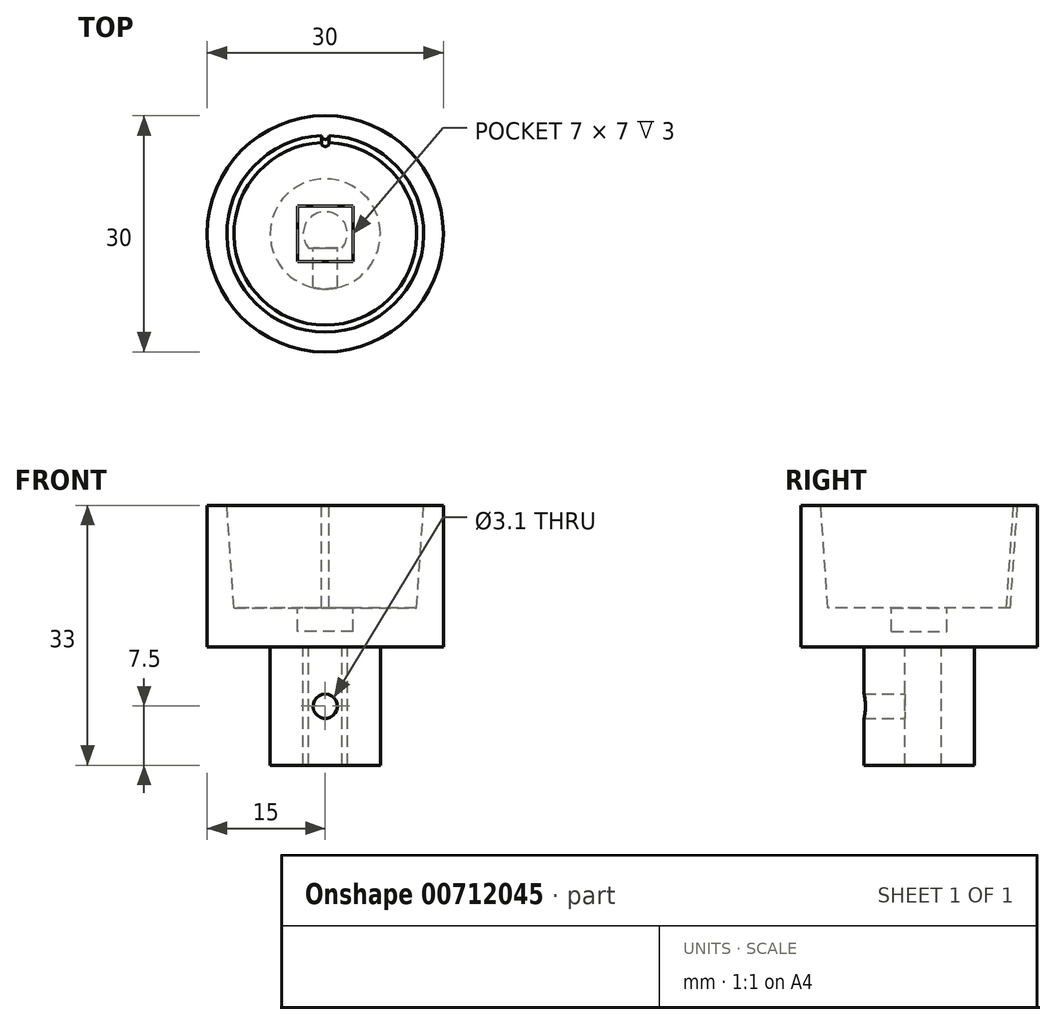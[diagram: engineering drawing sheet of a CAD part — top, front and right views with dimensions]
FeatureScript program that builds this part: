
annotation { "Feature Type Name" : "Feature", "Feature Type Description" : "" }
export const myFeature = defineFeature(function(context is Context, id is Id, definition is map)
    precondition{}
    {
        {
            var Q0;
            Q0=qCreatedBy(makeId("Top.planeOp"),FACE);
            var sketch = newSketch(context, id + "F0", { "sketchPlane" : qUnion([Q0])});
            skLineSegment(sketch, "E0", {"start": v(-2.14, -1.8) * mm, "end": v(2.14, -1.8) * mm});
            skArc(sketch, "E1", {"start": v(-2.14, -1.8) * mm, "mid": v(0, 2.8) * mm, "end": v(2.14, -1.8) * mm});
            skCircle(sketch, "E2", {"center": v(0, 0) * mm, "radius": 15 * mm});
            skCircle(sketch, "E3", {"center": v(0, 0) * mm, "radius": 7 * mm});
            skCircle(sketch, "E4", {"center": v(0, 0) * mm, "radius": 11.6 * mm});
            skSolve(sketch);
        }
        {
            var Q0;
            Q0=makeQuery(id+"F0.imprint","IMPRINT",FACE,{"disambiguationData":[TD([[makeQuery(id+"F0.imprint","IMPRINT",EDGE,{"derivedFrom":sQuery(id+"F0.wireOp",EDGE,"E0")}),-1.0]])]});
            var Q1;
            Q1=sQuery(id+"F0.wireOp",EDGE,"E1");
            var Q2;
            Q2=sQuery(id+"F0.wireOp",EDGE,"E0");
            extrude(context, id + "F1", {"entities" : qUnion([Q0]), "surfaceEntities" : qUnion([Q1, Q2]), "oppositeDirection" : true, "depth" : 15 * mm, "offsetDistance" : 25 * mm});
        }
        {
            var Q0;
            Q0=makeQuery(id+"F0.imprint","IMPRINT",FACE,{"disambiguationData":[TD([[makeQuery(id+"F0.imprint","IMPRINT",EDGE,{"derivedFrom":sQuery(id+"F0.wireOp",EDGE,"E3")}),-1.0]])]});
            var Q1;
            Q1=makeQuery(id+"F0.imprint","IMPRINT",FACE,{"disambiguationData":[TD([[makeQuery(id+"F0.imprint","IMPRINT",EDGE,{"derivedFrom":sQuery(id+"F0.wireOp",EDGE,"E0")}),1.0]])]});
            var Q2;
            Q2=makeQuery(id+"F0.imprint","IMPRINT",FACE,{"disambiguationData":[TD([[makeQuery(id+"F0.imprint","IMPRINT",EDGE,{"derivedFrom":sQuery(id+"F0.wireOp",EDGE,"E0")}),-1.0]])]});
            extrude(context, id + "F2", {"entities" : qUnion([Q0, Q1, Q2]), "operationType" : NewBodyOperationType.ADD, "depth" : 5 * mm, "offsetDistance" : 25 * mm});
        }
        {
            var Q0;
            {var subQ0=sQuery(id+"F0.wireOp",EDGE,"E0");Q0=makeQuery(id+"F2.boolean.opBoolean","MERGE",FACE,{"derivedFrom":[makeQuery(id+"F1.opExtrude","SWEPT_FACE",FACE,{"disambiguationData":[OSD([subQ0])]}),makeQuery(id+"F2.opExtrude","SWEPT_FACE",FACE,{"disambiguationData":[OSD([subQ0])]})]});}
            var sketch = newSketch(context, id + "F3", { "sketchPlane" : qUnion([Q0])});
            skPoint(sketch, "E5", {"position": v(0, -7.5) * mm});
            skSolve(sketch);
        }
        {
            var Q0;
            Q0=sQuery(id+"F3.wireOp",VERTEX,"E5");
            var Q1;
            Q1=makeQuery(id+"F1.opExtrude","SWEPT_BODY",BODY,{"disambiguationData":[OSD([sQuery(id+"F0.wireOp",EDGE,"E0"),sQuery(id+"F0.wireOp",EDGE,"E1"),sQuery(id+"F0.wireOp",EDGE,"E3")])]});
            hole(context, id + "F4", {"style" : HoleStyle.SIMPLE, "endStyle" : HoleEndStyle.THROUGH, "holeDiameter" : 3.1 * mm, "majorDiameter" : 5 * mm, "isTappedThrough" : true, "tappedDepth" : 12 * mm, "tapClearance" : 3, "locations" : qUnion([Q0]), "scope" : qUnion([Q1])});
        }
        {
            var Q0;
            Q0=makeQuery(id+"F2.opExtrude","CAP_FACE",FACE,{"disambiguationData":[OSD([sQuery(id+"F0.wireOp",EDGE,"E4"),sQuery(id+"F0.wireOp",EDGE,"QTVwVzxJ-1bkS-bkWT-XEsq-TVnwtJ6gXQn8")])],"isStart":false});
            var sketch = newSketch(context, id + "F5", { "sketchPlane" : qUnion([Q0])});
            skLineSegment(sketch, "E6.bottom", {"start": v(3.5, -3.5) * mm, "end": v(-3.5, -3.5) * mm});
            skLineSegment(sketch, "E6.top", {"start": v(3.5, 3.5) * mm, "end": v(-3.5, 3.5) * mm});
            skLineSegment(sketch, "E6.left", {"start": v(3.5, -3.5) * mm, "end": v(3.5, 3.5) * mm});
            skLineSegment(sketch, "E6.right", {"start": v(-3.5, -3.5) * mm, "end": v(-3.5, 3.5) * mm});
            skPoint(sketch, "E6.middle", {"position": v(0, 0) * mm});
            skSolve(sketch);
        }
        {
            var Q0;
            Q0=makeQuery(id+"F5.imprint","IMPRINT",FACE,{"disambiguationData":[TD([[makeQuery(id+"F5.imprint","IMPRINT",EDGE,{"derivedFrom":sQuery(id+"F5.wireOp",EDGE,"E6.bottom")}),-1.0]])]});
            extrude(context, id + "F6", {"entities" : qUnion([Q0]), "operationType" : NewBodyOperationType.REMOVE, "oppositeDirection" : true, "depth" : 3 * mm, "offsetDistance" : 25 * mm});
        }
        {
            var Q0;
            Q0=qCreatedBy(makeId("Right.planeOp"),FACE);
            var sketch = newSketch(context, id + "F7", { "sketchPlane" : qUnion([Q0])});
            skLineSegment(sketch, "E7", {"start": v(11.6, 0) * mm, "end": v(15, 0) * mm});
            skLineSegment(sketch, "E8", {"start": v(15, 18) * mm, "end": v(12.5, 18) * mm});
            skLineSegment(sketch, "E9", {"start": v(15, 18) * mm, "end": v(15, 0) * mm});
            skLineSegment(sketch, "E10", {"start": v(11.6, 0) * mm, "end": v(11.6, 5) * mm});
            skLineSegment(sketch, "E11", {"start": v(11.6, 5) * mm, "end": v(12.5, 18) * mm});
            skLineSegment(sketch, "E12", {"start": v(0, 9.96) * mm, "end": v(0, -1.49) * mm, "construction": true});
            skSolve(sketch);
        }
        {
            var Q0;
            Q0=makeQuery(id+"F7.imprint","IMPRINT",FACE,{"disambiguationData":[TD([[makeQuery(id+"F7.imprint","IMPRINT",EDGE,{"derivedFrom":sQuery(id+"F7.wireOp",EDGE,"E7")}),1.0]])]});
            var Q1;
            Q1=sQuery(id+"F7.wireOp",EDGE,"E12");
            revolve(context, id + "F8", {"operationType" : NewBodyOperationType.ADD, "surfaceOperationType" : NewSurfaceOperationType.NEW, "entities" : qUnion([Q0]), "axis" : qUnion([Q1]), "revolveType" : RevolveType.FULL});
        }
        {
            var Q0;
            Q0=makeQuery(id+"F5.imprint","IMPRINT",FACE,{"disambiguationData":[TD([[makeQuery(id+"F5.imprint","IMPRINT",EDGE,{"derivedFrom":sQuery(id+"F5.wireOp",EDGE,"E6.bottom")}),1.0]])]});
            var sketch = newSketch(context, id + "F9", { "sketchPlane" : qUnion([Q0])});
            skCircle(sketch, "E13", {"center": v(0, 0) * mm, "radius": 11.6 * mm, "construction": true});
            skArc(sketch, "E14", {"start": v(-0.5, 11.59) * mm, "mid": v(0, 11.1) * mm, "end": v(0.5, 11.59) * mm});
            skSolve(sketch);
        }
        {
            var Q0;
            Q0=makeQuery(id+"F8.opRevolve","SWEPT_FACE",FACE,{"disambiguationData":[OSD([sQuery(id+"F7.wireOp",EDGE,"E8")])]});
            var sketch = newSketch(context, id + "F10", { "sketchPlane" : qUnion([Q0])});
            skCircle(sketch, "E15", {"center": v(0, 0) * mm, "radius": 12.5 * mm, "construction": true});
            skArc(sketch, "E16", {"start": v(-0.5, 12.5) * mm, "mid": v(0, 12) * mm, "end": v(0.5, 12.5) * mm});
            skSolve(sketch);
        }
        {
            var Q1;
            {var subQ0=sQuery(id+"F9.wireOp",EDGE,"E14");Q1=makeQuery(id+"F9.imprint","IMPRINT",FACE,{"disambiguationData":[TD([[makeQuery(id+"F9.imprint","IMPRINT",EDGE,{"derivedFrom":subQ0}),1.0]])]});}
            var Q2;
            {var subQ0=sQuery(id+"F10.wireOp",EDGE,"E16");Q2=makeQuery(id+"F10.imprint","IMPRINT",FACE,{"disambiguationData":[TD([[makeQuery(id+"F10.imprint","IMPRINT",EDGE,{"derivedFrom":subQ0}),1.0]])]});}
            loft(context, id + "F11", {"operationType" : NewBodyOperationType.ADD, "sheetProfilesArray" : [{ "sheetProfileEntities" : qUnion([Q1]) }, { "sheetProfileEntities" : qUnion([Q2]) }]});
        }
    });
